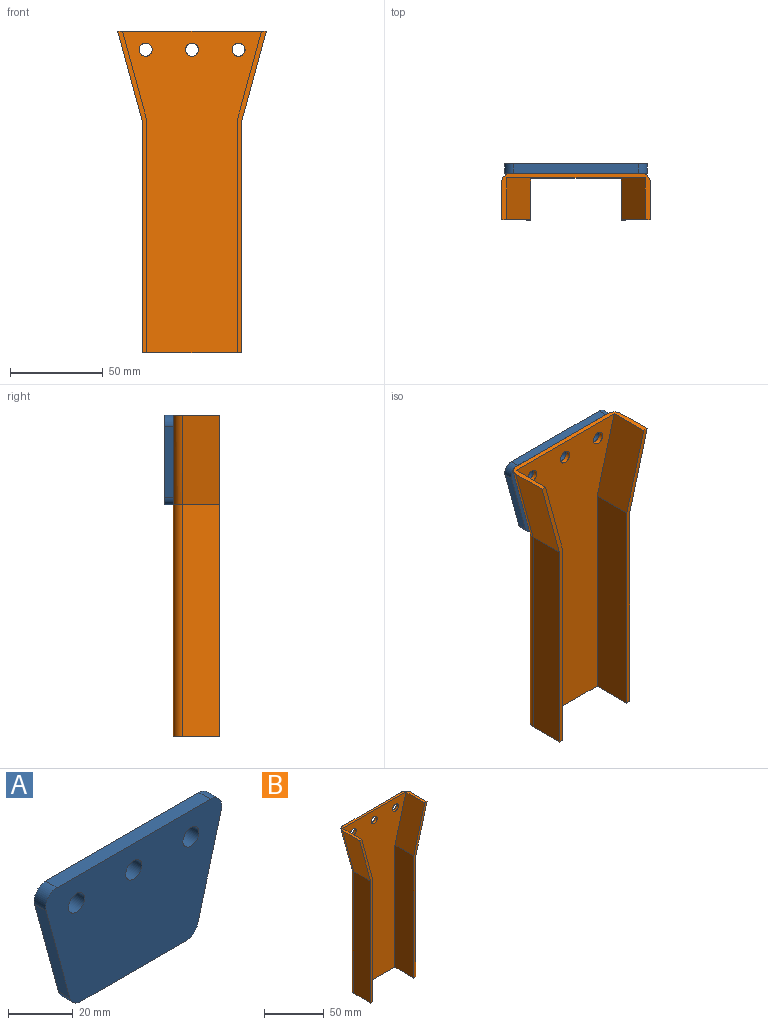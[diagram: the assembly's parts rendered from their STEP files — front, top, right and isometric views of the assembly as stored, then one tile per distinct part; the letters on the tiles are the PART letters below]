
ASSEMBLY  parts=2 mates=1
PART A: 13 faces, bbox 76.9x5x48.3 mm
  f0: plane 66.93x5mm, normal (0,0,1), area 334.6mm2, adj f7,f8,f9,f12
  f1: plane 38.25x10.41mm, normal (-0.96,0,-0.26), area 198.2mm2, adj f7,f8,f9,f10
  f2: plane 46.11x5mm, normal (0,0,-1), area 230.6mm2, adj f7,f8,f10,f11
  f3: cylinder r=3.5mm len=7mm, axis (0,1,0), area 110mm2, adj f7,f8
  f4: cylinder r=3.5mm len=7mm, axis (0,1,0), area 110mm2, adj f7,f8
  f5: cylinder r=3.5mm len=7mm, axis (0,1,0), area 110mm2, adj f7,f8
  f6: plane 38.25x10.41mm, normal (0.96,0,-0.26), area 198.2mm2, adj f7,f8,f11,f12
  f7: plane 76.93x48.25mm, normal (0,-1,0), area 3086.5mm2, adj f0,f1,f2,f3,f4,f5,f6,f9
  f8: plane 76.93x48.25mm, normal (0,1,0), area 3086.5mm2, adj f0,f1,f2,f3,f4,f5,f6,f9
  f9: cylinder r=5mm len=6.31mm, axis (0,-1,0), area 45.9mm2, adj f0,f1,f7,f8
  f10: cylinder r=5mm len=5mm, axis (0,1,0), area 32.6mm2, adj f1,f2,f7,f8
  f11: cylinder r=5mm len=5mm, axis (0,-1,0), area 32.6mm2, adj f2,f6,f7,f8
  f12: cylinder r=5mm len=6.31mm, axis (0,1,0), area 45.9mm2, adj f0,f6,f7,f8
PART B: 21 faces, bbox 80x25x174.6 mm
  f0: plane 173.31x15.63mm, normal (0,-1,0), area 437.7mm2, adj f2,f6,f7,f8,f12,f13
  f1: plane 173.3x15.64mm, normal (0,-1,0), area 437.6mm2, adj f2,f6,f9,f10,f14,f15
  f2: plane 80.02x25mm, normal (0,0,1), area 305.5mm2, adj f0,f1,f8,f9,f11,f13,f14,f16
  f3: cylinder r=3.51mm len=7.01mm, axis (0,1,0), area 55.1mm2, adj f11,f16
  f4: cylinder r=3.5mm len=7mm, axis (0,1,0), area 55mm2, adj f11,f16
  f5: cylinder r=3.5mm len=7mm, axis (0,1,0), area 55mm2, adj f11,f16
  f6: plane 53.75x25mm, normal (0,0,-1), area 236.1mm2, adj f0,f1,f7,f10,f11,f12,f15,f16
  f7: plane 125.06x20mm, normal (1,0,0), area 2501.3mm2, adj f0,f6,f8,f18
  f8: plane 48.25x20mm, normal (0.96,0,-0.26), area 1000.1mm2, adj f0,f2,f7,f17
  f9: plane 48.25x20mm, normal (-0.96,0,-0.26), area 1000.1mm2, adj f1,f2,f10,f19
  f10: plane 125.05x20mm, normal (-1,0,0), area 2501mm2, adj f1,f6,f9,f20
  f11: plane 173.31x69.66mm, normal (0,1,0), area 8083.2mm2, adj f2,f3,f4,f5,f6,f17,f18,f19
  f12: plane 125.4x22.5mm, normal (-1,0,0), area 2821.4mm2, adj f0,f6,f13,f16
  f13: plane 47.92x22.5mm, normal (-0.96,0,0.26), area 1117.3mm2, adj f0,f2,f12,f16
  f14: plane 47.92x22.5mm, normal (0.96,0,0.26), area 1117.4mm2, adj f1,f2,f15,f16
  f15: plane 125.39x22.5mm, normal (1,0,0), area 2821.2mm2, adj f1,f6,f14,f16
  f16: plane 173.31x74.84mm, normal (0,-1,0), area 8958.4mm2, adj f2,f3,f4,f5,f6,f12,f13,f14
  f17: cylinder r=5mm len=50.21mm, axis (0.26,0,0.96), area 390.8mm2, adj f2,f8,f11,f18
  f18: cylinder r=5mm len=125.73mm, axis (0,0,1), area 984.2mm2, adj f6,f7,f11,f17
  f19: cylinder r=5mm len=50.21mm, axis (0.26,0,-0.96), area 390.8mm2, adj f2,f9,f11,f20
  f20: cylinder r=5mm len=125.72mm, axis (0,0,-1), area 984.1mm2, adj f6,f10,f11,f19
PLACE A t=(-87.34,20.57,21.35)mm
PLACE B t=(-85.37,15.57,20.05)mm
MATE slider A.f3 <-> B.f3  axis (0,1,0) through (-96.12,20.57,32.36)mm
